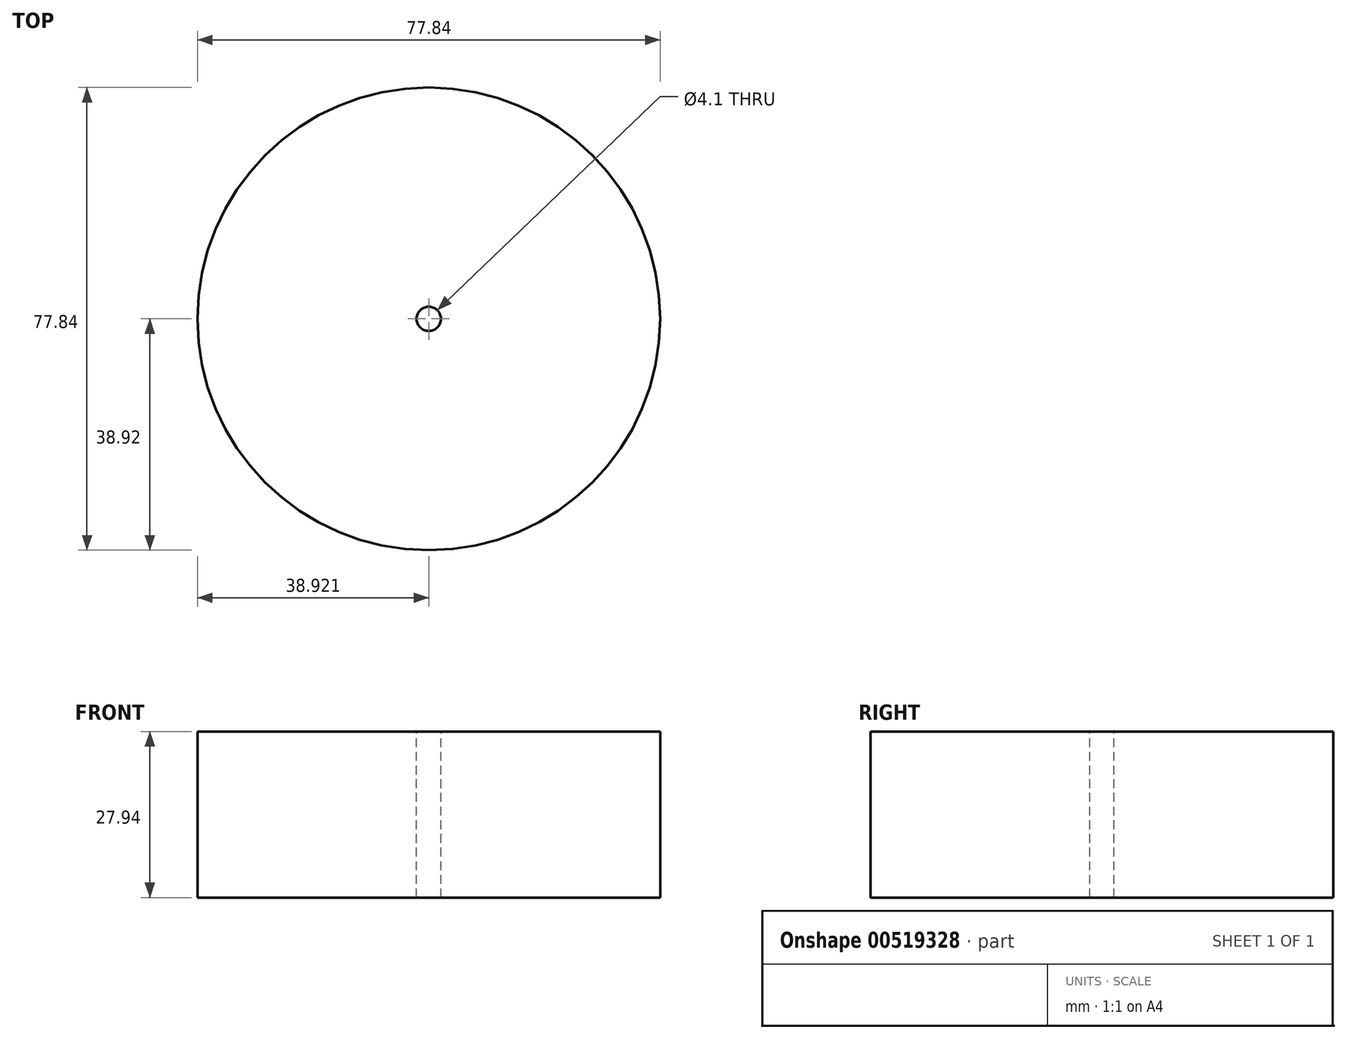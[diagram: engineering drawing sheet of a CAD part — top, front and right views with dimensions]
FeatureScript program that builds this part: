
annotation { "Feature Type Name" : "Feature", "Feature Type Description" : "" }
export const myFeature = defineFeature(function(context is Context, id is Id, definition is map)
    precondition{}
    {
        {
            var Q0;
            Q0=qCreatedBy(makeId("Top.planeOp"),FACE);
            var sketch = newSketch(context, id + "F0", { "sketchPlane" : qUnion([Q0])});
            skCircle(sketch, "E0", {"center": v(-49.26, -49.3) * mm, "radius": 38.92 * mm});
            skSolve(sketch);
        }
        {
            var Q0;
            Q0 = qSketchRegion(id + "F0", true);
            extrude(context, id + "F1", {"entities" : qUnion([Q0]), "depth" : 27.94 * mm, "offsetDistance" : 25.4 * mm});
        }
        {
            var Q0;
            Q0=makeQuery(id+"F1.opExtrude","CAP_FACE",FACE,{"disambiguationData":[OSD([sQuery(id+"F0.wireOp",EDGE,"E0")])],"isStart":false});
            var sketch = newSketch(context, id + "F2", { "sketchPlane" : qUnion([Q0])});
            skCircle(sketch, "E1", {"center": v(-49.26, -49.3) * mm, "radius": 2.05 * mm});
            skSolve(sketch);
        }
        {
            var Q0;
            Q0=makeQuery(id+"F2.imprint","IMPRINT",FACE,{"disambiguationData":[TD([[makeQuery(id+"F2.imprint","IMPRINT",EDGE,{"derivedFrom":sQuery(id+"F2.wireOp",EDGE,"E1")}),1.0]])]});
            extrude(context, id + "F3", {"entities" : qUnion([Q0]), "operationType" : NewBodyOperationType.REMOVE, "endBound" : BoundingType.UP_TO_NEXT, "oppositeDirection" : true, "depth" : 25.4 * mm, "offsetDistance" : 25.4 * mm});
        }
    });
